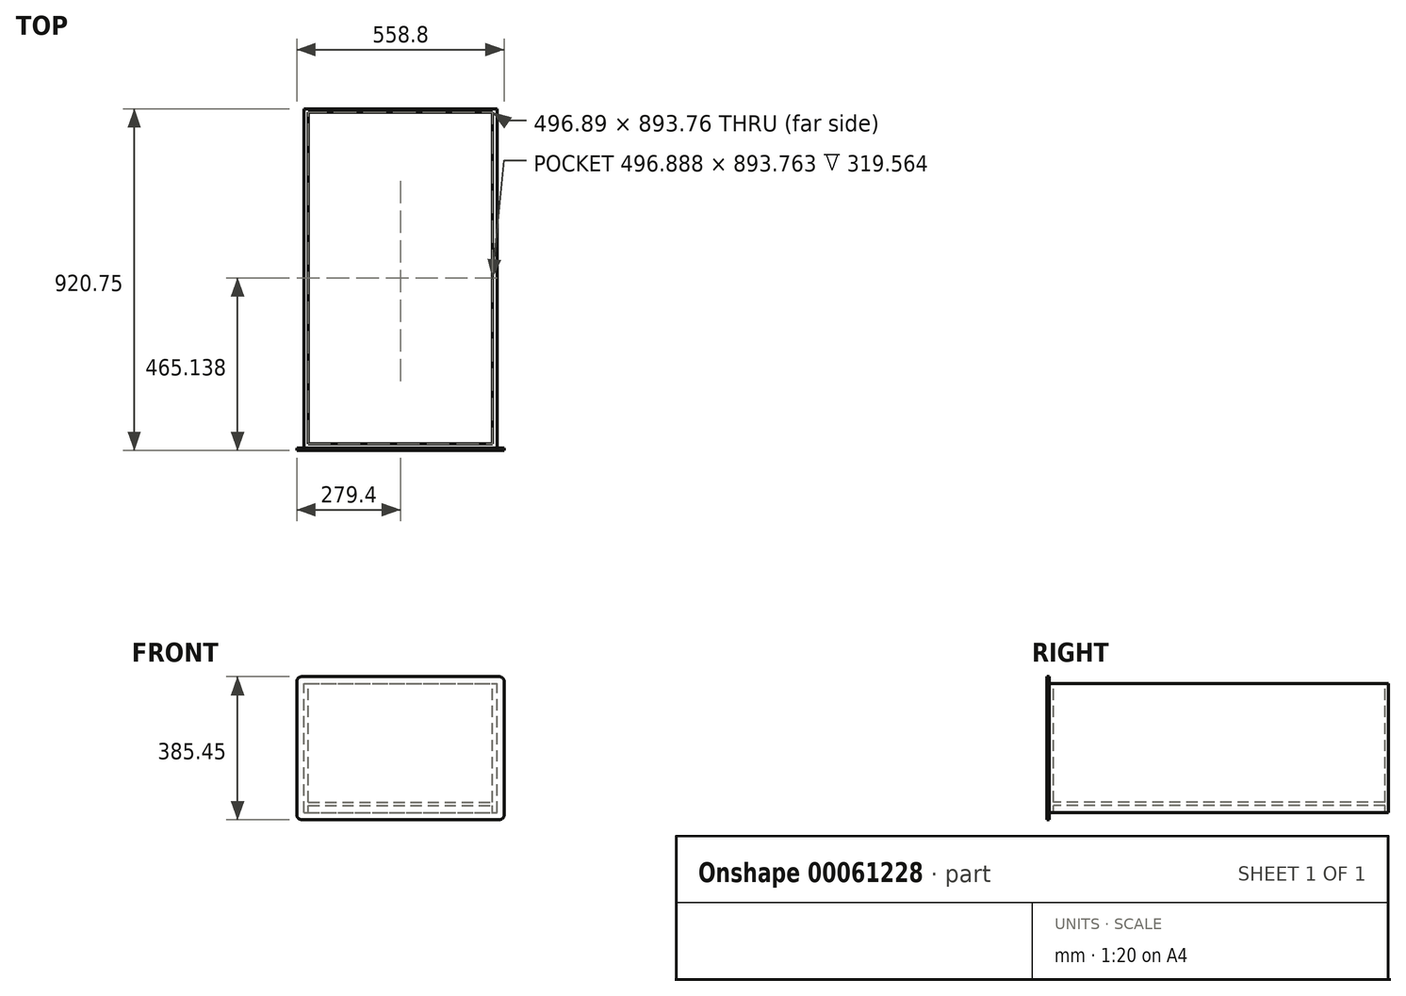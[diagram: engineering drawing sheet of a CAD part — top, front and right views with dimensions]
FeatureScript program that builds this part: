
annotation { "Feature Type Name" : "Feature", "Feature Type Description" : "" }
export const myFeature = defineFeature(function(context is Context, id is Id, definition is map)
    precondition{}
    {
        {
            var Q0;
            Q0=qCreatedBy(makeId("Front.planeOp"),FACE);
            var sketch = newSketch(context, id + "F0", { "sketchPlane" : qUnion([Q0])});
            skLineSegment(sketch, "E0.bottom", {"start": v(0, 0) * mm, "end": v(520.7, 0) * mm});
            skLineSegment(sketch, "E0.top", {"start": v(0, 347.35) * mm, "end": v(520.7, 347.35) * mm});
            skLineSegment(sketch, "E0.left", {"start": v(0, 0) * mm, "end": v(0, 347.35) * mm});
            skLineSegment(sketch, "E0.right", {"start": v(520.7, 0) * mm, "end": v(520.7, 347.35) * mm});
            skSolve(sketch);
        }
        {
            var Q0;
            Q0 = qSketchRegion(id + "F0", true);
            extrude(context, id + "F1", {"entities" : qUnion([Q0]), "depth" : 914.4 * mm});
        }
        {
            var Q0;
            Q0=makeQuery(id+"F1.opExtrude","SWEPT_FACE",FACE,{"disambiguationData":[OSD([sQuery(id+"F0.wireOp",EDGE,"E0.top")])]});
            var Q1;
            Q1=makeQuery(id+"F1.opExtrude","SWEPT_FACE",FACE,{"disambiguationData":[OSD([sQuery(id+"F0.wireOp",EDGE,"E0.bottom")])]});
            shell(context, id + "F2", {"entities" : qUnion([Q0, Q1]), "thickness" : 11.9 * mm});
        }
        {
            var Q0;
            Q0=makeQuery(id+"F1.opExtrude","CAP_FACE",FACE,{"disambiguationData":[OSD([sQuery(id+"F0.wireOp",EDGE,"E0.bottom"),sQuery(id+"F0.wireOp",EDGE,"E0.top"),sQuery(id+"F0.wireOp",EDGE,"E0.left"),sQuery(id+"F0.wireOp",EDGE,"E0.right")])],"isStart":false});
            var sketch = newSketch(context, id + "F3", { "sketchPlane" : qUnion([Q0])});
            skLineSegment(sketch, "E1.0", {"start": v(-6.35, -19.05) * mm, "end": v(527.05, -19.05) * mm});
            skLineSegment(sketch, "E1.1", {"start": v(-19.05, -6.35) * mm, "end": v(-19.05, 353.7) * mm});
            skLineSegment(sketch, "E1.2", {"start": v(-6.35, 366.4) * mm, "end": v(527.05, 366.4) * mm});
            skLineSegment(sketch, "E1.3", {"start": v(539.75, -6.35) * mm, "end": v(539.75, 353.7) * mm});
            skPoint(sketch, "E2.visualSharp", {"position": v(-19.05, 366.4) * mm});
            skArc(sketch, "E2.filletArc", {"start": v(-6.35, 366.4) * mm, "mid": v(-15.33, 362.68) * mm, "end": v(-19.05, 353.7) * mm});
            skPoint(sketch, "E3.visualSharp", {"position": v(539.75, -19.05) * mm});
            skArc(sketch, "E3.filletArc", {"start": v(527.05, -19.05) * mm, "mid": v(536.03, -15.33) * mm, "end": v(539.75, -6.35) * mm});
            skPoint(sketch, "E4.visualSharp", {"position": v(-19.05, -19.05) * mm});
            skArc(sketch, "E4.filletArc", {"start": v(-19.05, -6.35) * mm, "mid": v(-15.33, -15.33) * mm, "end": v(-6.35, -19.05) * mm});
            skPoint(sketch, "E5.visualSharp", {"position": v(539.75, 366.4) * mm});
            skArc(sketch, "E5.filletArc", {"start": v(539.75, 353.7) * mm, "mid": v(536.03, 362.68) * mm, "end": v(527.05, 366.4) * mm});
            skSolve(sketch);
        }
        {
            var Q0;
            Q0 = qSketchRegion(id + "F3", true);
            extrude(context, id + "F4", {"entities" : qUnion([Q0]), "operationType" : NewBodyOperationType.ADD, "depth" : 6.35 * mm});
        }
        {
            var Q0;
            Q0=makeQuery(id+"F1.opExtrude","SWEPT_FACE",FACE,{"disambiguationData":[OSD([sQuery(id+"F0.wireOp",EDGE,"E0.top")])]});
            var sketch = newSketch(context, id + "F5", { "sketchPlane" : qUnion([Q0])});
            skLineSegment(sketch, "E6.bottom", {"start": v(11.9, -11.9) * mm, "end": v(508.8, -11.9) * mm});
            skLineSegment(sketch, "E6.top", {"start": v(11.9, -8.73) * mm, "end": v(508.8, -8.73) * mm});
            skLineSegment(sketch, "E6.left", {"start": v(11.9, -11.9) * mm, "end": v(11.9, -8.73) * mm});
            skLineSegment(sketch, "E6.right", {"start": v(508.8, -11.9) * mm, "end": v(508.8, -8.73) * mm});
            skSolve(sketch);
        }
        {
            var Q0;
            Q0 = qSketchRegion(id + "F5", true);
            extrude(context, id + "F6", {"entities" : qUnion([Q0]), "operationType" : NewBodyOperationType.REMOVE, "endBound" : BoundingType.THROUGH_ALL, "oppositeDirection" : true, "depth" : 25.4 * mm});
        }
        {
            var Q0;
            Q0=makeQuery(id+"F1.opExtrude","CAP_FACE",FACE,{"disambiguationData":[OSD([sQuery(id+"F0.wireOp",EDGE,"E0.bottom"),sQuery(id+"F0.wireOp",EDGE,"E0.top"),sQuery(id+"F0.wireOp",EDGE,"E0.left"),sQuery(id+"F0.wireOp",EDGE,"E0.right")])],"isStart":true});
            var sketch = newSketch(context, id + "F7", { "sketchPlane" : qUnion([Q0])});
            skLineSegment(sketch, "E7.bottom", {"start": v(-511.97, 19.05) * mm, "end": v(-8.73, 19.05) * mm});
            skLineSegment(sketch, "E7.top", {"start": v(-511.97, 27.78) * mm, "end": v(-8.73, 27.78) * mm});
            skLineSegment(sketch, "E7.left", {"start": v(-511.97, 19.05) * mm, "end": v(-511.97, 27.78) * mm});
            skLineSegment(sketch, "E7.right", {"start": v(-8.73, 19.05) * mm, "end": v(-8.73, 27.78) * mm});
            skSolve(sketch);
        }
        {
            var Q0;
            Q0 = qSketchRegion(id + "F7", true);
            var Q1;
            Q1=makeQuery(id+"F4.opExtrude","CAP_FACE",FACE,{"disambiguationData":[OSD([sQuery(id+"F3.wireOp",EDGE,"E1.0"),sQuery(id+"F3.wireOp",EDGE,"E1.1"),sQuery(id+"F3.wireOp",EDGE,"E1.2"),sQuery(id+"F3.wireOp",EDGE,"E1.3"),sQuery(id+"F3.wireOp",EDGE,"E2.filletArc"),sQuery(id+"F3.wireOp",EDGE,"E3.filletArc"),sQuery(id+"F3.wireOp",EDGE,"E4.filletArc"),sQuery(id+"F3.wireOp",EDGE,"E5.filletArc")])],"isStart":true});
            extrude(context, id + "F8", {"entities" : qUnion([Q0]), "operationType" : NewBodyOperationType.ADD, "endBound" : BoundingType.UP_TO_SURFACE, "oppositeDirection" : true, "endBoundEntityFace" : qUnion([Q1]), "depth" : 25.4 * mm});
        }
    });
